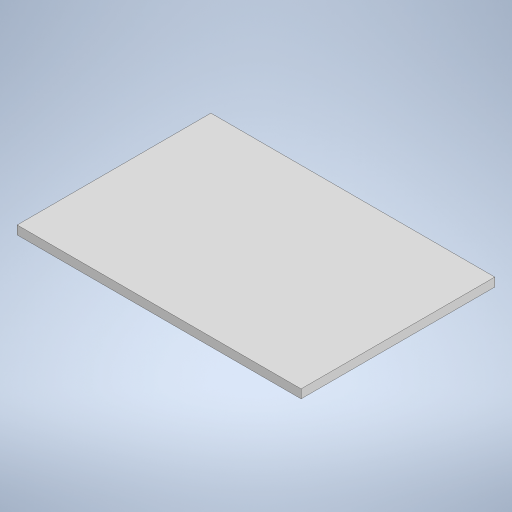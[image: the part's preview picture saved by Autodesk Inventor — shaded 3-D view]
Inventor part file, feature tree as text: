
AUTODESK INVENTOR PART (.ipt)
format: ipt  version: 2024 (Build 280153000, 153)  size: 201,728 bytes
history: native  units: mm
features: extrude x1, sketch x1
ambient origin geometry x8: Origin, YZ Plane, XZ Plane, XY Plane, X Axis, Y Axis, Z Axis, Center Point
bodies: Solid1 (feature_tree)
feature tree (2):
  extrude  "Extrusion1"  Depth=70.0mm
  sketch  "Sketch1"  dims[d0=102.6mm d1=70.0mm d2=3.125mm d3=0.0mm]
